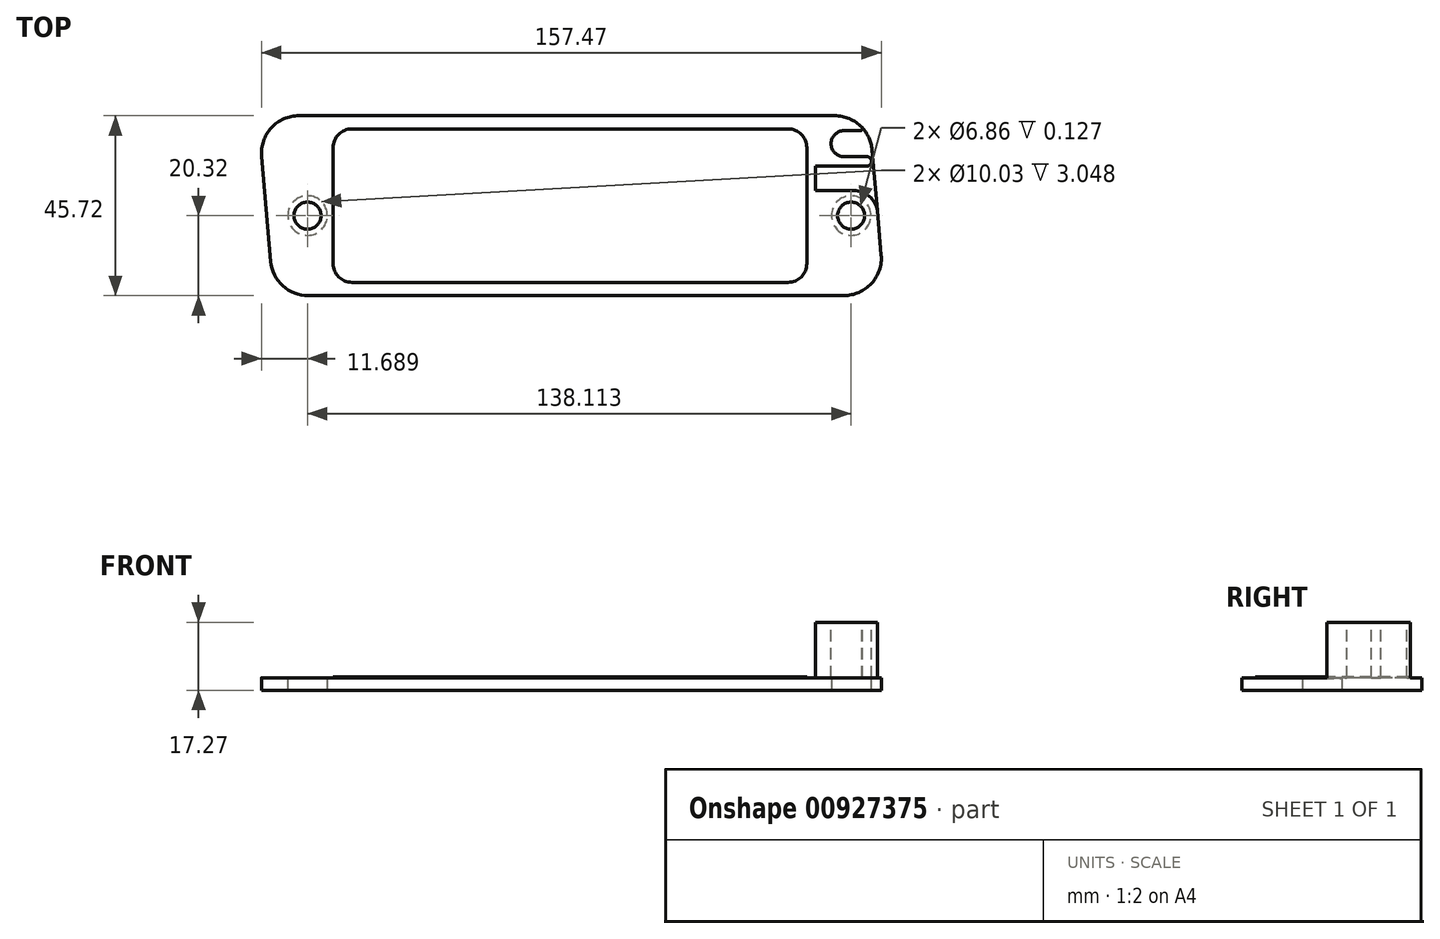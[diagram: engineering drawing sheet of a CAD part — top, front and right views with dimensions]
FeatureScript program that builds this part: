
annotation { "Feature Type Name" : "Feature", "Feature Type Description" : "" }
export const myFeature = defineFeature(function(context is Context, id is Id, definition is map)
    precondition{}
    {
        {
            var Q0;
            Q0=qCreatedBy(makeId("Top.planeOp"),FACE);
            var sketch = newSketch(context, id + "F0", { "sketchPlane" : qUnion([Q0])});
            skLineSegment(sketch, "E0.bottom", {"start": v(-68.04, 22.86) * mm, "end": v(68.04, 22.86) * mm});
            skLineSegment(sketch, "E0.top", {"start": v(-65.71, -22.86) * mm, "end": v(70.38, -22.86) * mm});
            skPoint(sketch, "E1", {"position": v(0, 22.86) * mm});
            skArc(sketch, "E2", {"start": v(77.53, 14.17) * mm, "mid": v(74.48, 20.36) * mm, "end": v(68.04, 22.86) * mm});
            skLineSegment(sketch, "E3", {"start": v(77.53, 14.17) * mm, "end": v(79.87, -12.5) * mm});
            skLineSegment(sketch, "E4", {"start": v(77.53, 14.17) * mm, "end": v(77.53, -3.79) * mm, "construction": true});
            skArc(sketch, "E5", {"start": v(70.38, -22.86) * mm, "mid": v(77.4, -19.77) * mm, "end": v(79.87, -12.5) * mm});
            skArc(sketch, "E6", {"start": v(-68.04, 22.86) * mm, "mid": v(-75.07, 19.77) * mm, "end": v(-77.53, 12.5) * mm});
            skLineSegment(sketch, "E7", {"start": v(-77.53, 12.5) * mm, "end": v(-75.2, -14.17) * mm});
            skLineSegment(sketch, "E8", {"start": v(-77.53, 12.5) * mm, "end": v(-77.53, -10.9) * mm, "construction": true});
            skArc(sketch, "E9", {"start": v(-75.2, -14.17) * mm, "mid": v(-72.15, -20.36) * mm, "end": v(-65.71, -22.86) * mm});
            skSolve(sketch);
        }
        {
            var Q0;
            Q0=makeQuery(id+"F0.imprint","IMPRINT",FACE,{"disambiguationData":[TD([[makeQuery(id+"F0.imprint","IMPRINT",EDGE,{"derivedFrom":sQuery(id+"F0.wireOp",EDGE,"E0.bottom")}),-1.0]])]});
            extrude(context, id + "F1", {"entities" : qUnion([Q0]), "depth" : 17.27 * mm, "offsetDistance" : 25.4 * mm});
        }
        {
            var Q0;
            Q0=makeQuery(id+"F1.opExtrude","CAP_FACE",FACE,{"disambiguationData":[OSD([sQuery(id+"F0.wireOp",EDGE,"E0.bottom"),sQuery(id+"F0.wireOp",EDGE,"E0.top"),sQuery(id+"F0.wireOp",EDGE,"E2"),sQuery(id+"F0.wireOp",EDGE,"E3"),sQuery(id+"F0.wireOp",EDGE,"E5"),sQuery(id+"F0.wireOp",EDGE,"E6"),sQuery(id+"F0.wireOp",EDGE,"E7"),sQuery(id+"F0.wireOp",EDGE,"E9")])],"isStart":false});
            var sketch = newSketch(context, id + "F2", { "sketchPlane" : qUnion([Q0])});
            skLineSegment(sketch, "E10.bottom", {"start": v(-54.61, 19.5) * mm, "end": v(56.2, 19.5) * mm});
            skLineSegment(sketch, "E10.top", {"start": v(-54.61, -19.5) * mm, "end": v(56.2, -19.5) * mm});
            skLineSegment(sketch, "E10.left", {"start": v(-59.37, 14.73) * mm, "end": v(-59.37, -14.73) * mm});
            skLineSegment(sketch, "E10.right", {"start": v(60.96, 14.73) * mm, "end": v(60.96, -14.73) * mm});
            skPoint(sketch, "E11", {"position": v(-59.37, 0) * mm});
            skPoint(sketch, "E12.visualSharp", {"position": v(-59.37, 19.5) * mm});
            skArc(sketch, "E12.filletArc", {"start": v(-54.61, 19.5) * mm, "mid": v(-57.98, 18.1) * mm, "end": v(-59.37, 14.73) * mm});
            skPoint(sketch, "E13.visualSharp", {"position": v(-59.37, -19.5) * mm});
            skArc(sketch, "E13.filletArc", {"start": v(-59.37, -14.73) * mm, "mid": v(-57.98, -18.1) * mm, "end": v(-54.61, -19.5) * mm});
            skPoint(sketch, "E14.visualSharp", {"position": v(60.96, -19.5) * mm});
            skArc(sketch, "E14.filletArc", {"start": v(56.2, -19.5) * mm, "mid": v(59.57, -18.1) * mm, "end": v(60.96, -14.73) * mm});
            skPoint(sketch, "E15.visualSharp", {"position": v(60.96, 19.5) * mm});
            skArc(sketch, "E15.filletArc", {"start": v(60.96, 14.73) * mm, "mid": v(59.57, 18.1) * mm, "end": v(56.2, 19.5) * mm});
            skPoint(sketch, "E16", {"position": v(0, -2.54) * mm});
            skSolve(sketch);
        }
        {
            var Q0;
            Q0=makeQuery(id+"F2.imprint","IMPRINT",FACE,{"disambiguationData":[TD([[makeQuery(id+"F2.imprint","IMPRINT",EDGE,{"derivedFrom":sQuery(id+"F2.wireOp",EDGE,"E10.bottom")}),-1.0]])]});
            extrude(context, id + "F3", {"entities" : qUnion([Q0]), "operationType" : NewBodyOperationType.REMOVE, "oppositeDirection" : true, "depth" : 13.84 * mm, "offsetDistance" : 25.4 * mm});
        }
        {
            var Q0;
            Q0=makeQuery(id+"F1.opExtrude","CAP_FACE",FACE,{"disambiguationData":[OSD([sQuery(id+"F0.wireOp",EDGE,"E0.bottom"),sQuery(id+"F0.wireOp",EDGE,"E0.top"),sQuery(id+"F0.wireOp",EDGE,"E2"),sQuery(id+"F0.wireOp",EDGE,"E3"),sQuery(id+"F0.wireOp",EDGE,"E5"),sQuery(id+"F0.wireOp",EDGE,"E6"),sQuery(id+"F0.wireOp",EDGE,"E7"),sQuery(id+"F0.wireOp",EDGE,"E9")])],"isStart":false});
            var sketch = newSketch(context, id + "F4", { "sketchPlane" : qUnion([Q0])});
            skLineSegment(sketch, "E17", {"start": v(-63.18, 10.03) * mm, "end": v(-76.22, 10.03) * mm});
            skLineSegment(sketch, "E18", {"start": v(-63.18, 10.03) * mm, "end": v(-63.18, 3.8) * mm});
            skLineSegment(sketch, "E19", {"start": v(-63.18, 3.81) * mm, "end": v(-72.92, 3.81) * mm});
            skLineSegment(sketch, "E20", {"start": v(-63.18, -8.25) * mm, "end": v(-72.7, -8.26) * mm});
            skPoint(sketch, "E21", {"position": v(0, -2.54) * mm});
            skArc(sketch, "E22", {"start": v(-72.92, 3.81) * mm, "mid": v(-76.24, -2.28) * mm, "end": v(-72.7, -8.25) * mm});
            skPoint(sketch, "E23", {"position": v(-76.24, -2.28) * mm});
            skLineSegment(sketch, "E24", {"start": v(-63.18, -8.26) * mm, "end": v(-63.18, -14.73) * mm});
            skArc(sketch, "E25", {"start": v(-63.18, -14.73) * mm, "mid": v(-60.8, -20.48) * mm, "end": v(-55.05, -22.86) * mm});
            skLineSegment(sketch, "E26", {"start": v(-76.22, 12.45) * mm, "end": v(-70.42, 12.45) * mm});
            skArc(sketch, "E27", {"start": v(-76.22, 12.45) * mm, "mid": v(-77.42, 11.24) * mm, "end": v(-76.22, 10.03) * mm});
            skPoint(sketch, "E28", {"position": v(-77.42, 11.24) * mm});
            skArc(sketch, "E29", {"start": v(-70.42, 12.45) * mm, "mid": v(-67.12, 15.75) * mm, "end": v(-70.42, 19.05) * mm});
            skLineSegment(sketch, "E30", {"start": v(-70.42, 19.05) * mm, "end": v(-74.57, 19.05) * mm});
            skArc(sketch, "E31", {"start": v(-68.04, 22.86) * mm, "mid": v(-71.8, 22.1) * mm, "end": v(-74.94, 19.9) * mm});
            skLineSegment(sketch, "E32", {"start": v(-68.04, 22.86) * mm, "end": v(-80.53, 22.86) * mm});
            skLineSegment(sketch, "E33", {"start": v(-80.53, 22.86) * mm, "end": v(-80.53, -22.86) * mm});
            skLineSegment(sketch, "E34", {"start": v(-80.53, -22.86) * mm, "end": v(-55.05, -22.86) * mm});
            skPoint(sketch, "E35.visualSharp", {"position": v(-75.66, 19.05) * mm});
            skArc(sketch, "E35.filletArc", {"start": v(-74.94, 19.9) * mm, "mid": v(-75.04, 19.36) * mm, "end": v(-74.57, 19.05) * mm});
            skPoint(sketch, "E36", {"position": v(-67.12, 15.75) * mm});
            skLineSegment(sketch, "E37", {"start": v(0, 45.68) * mm, "end": v(0, -48.97) * mm, "construction": true});
            skArc(sketch, "E38.MirrorCS", {"start": v(74.94, 19.9) * mm, "mid": v(75.04, 19.36) * mm, "end": v(74.57, 19.05) * mm});
            skLineSegment(sketch, "E39.MirrorCS", {"start": v(70.42, 19.05) * mm, "end": v(74.57, 19.05) * mm});
            skArc(sketch, "E40.MirrorCS", {"start": v(76.22, 12.45) * mm, "mid": v(77.42, 11.24) * mm, "end": v(76.22, 10.03) * mm});
            skLineSegment(sketch, "E41.MirrorCS", {"start": v(63.18, -8.25) * mm, "end": v(72.7, -8.25) * mm});
            skLineSegment(sketch, "E42.MirrorCS", {"start": v(63.18, 3.81) * mm, "end": v(72.92, 3.81) * mm});
            skLineSegment(sketch, "E43.MirrorCS", {"start": v(76.22, 12.45) * mm, "end": v(70.42, 12.45) * mm});
            skArc(sketch, "E44.MirrorCS", {"start": v(70.42, 12.45) * mm, "mid": v(67.12, 15.75) * mm, "end": v(70.42, 19.05) * mm});
            skLineSegment(sketch, "E45.MirrorCS", {"start": v(80.53, 22.86) * mm, "end": v(80.53, -22.86) * mm});
            skPoint(sketch, "E46.MirrorP", {"position": v(67.12, 15.75) * mm});
            skPoint(sketch, "E47.MirrorP", {"position": v(75.66, 19.05) * mm});
            skArc(sketch, "E48.MirrorCS", {"start": v(63.18, -14.73) * mm, "mid": v(60.8, -20.48) * mm, "end": v(55.05, -22.86) * mm});
            skPoint(sketch, "E49.MirrorP", {"position": v(77.42, 11.24) * mm});
            skArc(sketch, "E50.MirrorCS", {"start": v(72.92, 3.81) * mm, "mid": v(78.96, -2.33) * mm, "end": v(72.7, -8.26) * mm});
            skLineSegment(sketch, "E51.MirrorCS", {"start": v(63.18, 10.03) * mm, "end": v(76.22, 10.03) * mm});
            skLineSegment(sketch, "E52.MirrorCS", {"start": v(63.18, 10.03) * mm, "end": v(63.18, 3.8) * mm});
            skLineSegment(sketch, "E53.MirrorCS", {"start": v(80.53, -22.86) * mm, "end": v(55.05, -22.86) * mm});
            skLineSegment(sketch, "E54.MirrorCS", {"start": v(63.18, -8.26) * mm, "end": v(63.18, -14.73) * mm});
            skLineSegment(sketch, "E55.MirrorCS", {"start": v(68.04, 22.86) * mm, "end": v(80.53, 22.86) * mm});
            skArc(sketch, "E56.MirrorCS", {"start": v(68.04, 22.86) * mm, "mid": v(71.8, 22.1) * mm, "end": v(74.94, 19.9) * mm});
            skPoint(sketch, "E57", {"position": v(78.96, -2.11) * mm});
            skPoint(sketch, "E57.positionSnap0", {"position": v(78.96, -2.33) * mm});
            skSolve(sketch);
        }
        {
            var Q0;
            {var subQ8=sQuery(id+"F4.wireOp",EDGE,"E31");Q0=makeQuery(id+"F4.imprint","IMPRINT",FACE,{"disambiguationData":[TD([[makeQuery(id+"F4.imprint","IMPRINT",EDGE,{"derivedFrom":subQ8}),-1.0]])]});}
            var Q1;
            {var subQ1=sQuery(id+"F4.wireOp",EDGE,"E26");Q1=makeQuery(id+"F4.imprint","IMPRINT",FACE,{"disambiguationData":[TD([[makeQuery(id+"F4.imprint","IMPRINT",EDGE,{"derivedFrom":subQ1}),1.0]])]});}
            var Q2;
            {var subQ5=sQuery(id+"F4.wireOp",EDGE,"E17");Q2=makeQuery(id+"F4.imprint","IMPRINT",FACE,{"disambiguationData":[TD([[makeQuery(id+"F4.imprint","IMPRINT",EDGE,{"derivedFrom":subQ5}),1.0]])]});}
            var Q3;
            {var subQ4=sQuery(id+"F4.wireOp",EDGE,"E20");Q3=makeQuery(id+"F4.imprint","IMPRINT",FACE,{"disambiguationData":[TD([[makeQuery(id+"F4.imprint","IMPRINT",EDGE,{"derivedFrom":subQ4}),1.0]])]});}
            var Q4;
            {var subQ0=sQuery(id+"F4.wireOp",EDGE,"85b55b84-e163-4874-8427-2380d430c36f0.MirrorCS");Q4=makeQuery(id+"F4.imprint","IMPRINT",FACE,{"disambiguationData":[TD([[makeQuery(id+"F4.imprint","IMPRINT",EDGE,{"derivedFrom":subQ0}),1.0]])]});}
            var Q5;
            {var subQ3=sQuery(id+"F4.wireOp",EDGE,"af567ee6-1c98-437c-b070-15830dda8ad00.MirrorCS");Q5=makeQuery(id+"F4.imprint","IMPRINT",FACE,{"disambiguationData":[TD([[makeQuery(id+"F4.imprint","IMPRINT",EDGE,{"derivedFrom":subQ3}),-1.0]])]});}
            var Q6;
            {var subQ4=sQuery(id+"F4.wireOp",EDGE,"E41.MirrorCS");Q6=makeQuery(id+"F4.imprint","IMPRINT",FACE,{"disambiguationData":[TD([[makeQuery(id+"F4.imprint","IMPRINT",EDGE,{"derivedFrom":subQ4}),-1.0]])]});}
            var Q7;
            {var subQ3=sQuery(id+"F4.wireOp",EDGE,"E38.MirrorCS");Q7=makeQuery(id+"F4.imprint","IMPRINT",FACE,{"disambiguationData":[TD([[makeQuery(id+"F4.imprint","IMPRINT",EDGE,{"derivedFrom":subQ3}),1.0]])]});}
            extrude(context, id + "F5", {"entities" : qUnion([Q0, Q1, Q2, Q3, Q4, Q5, Q6, Q7]), "operationType" : NewBodyOperationType.REMOVE, "oppositeDirection" : true, "depth" : 14.1 * mm, "offsetDistance" : 25.4 * mm});
        }
        {
            var Q0;
            Q0=makeQuery(id+"F1.opExtrude","CAP_FACE",FACE,{"disambiguationData":[OSD([sQuery(id+"F0.wireOp",EDGE,"E0.bottom"),sQuery(id+"F0.wireOp",EDGE,"E0.top"),sQuery(id+"F0.wireOp",EDGE,"E2"),sQuery(id+"F0.wireOp",EDGE,"E3"),sQuery(id+"F0.wireOp",EDGE,"E5"),sQuery(id+"F0.wireOp",EDGE,"E6"),sQuery(id+"F0.wireOp",EDGE,"E7"),sQuery(id+"F0.wireOp",EDGE,"E9")])],"isStart":true});
            var sketch = newSketch(context, id + "F6", { "sketchPlane" : qUnion([Q0])});
            skLineSegment(sketch, "E58", {"start": v(72.23, 2.54) * mm, "end": v(-65.88, 2.54) * mm, "construction": true});
            skPoint(sketch, "E59", {"position": v(0, 2.54) * mm});
            skSolve(sketch);
        }
        {
            var Q0;
            Q0=sQuery(id+"F6.wireOp",VERTEX,"E58.start");
            var Q1;
            Q1=sQuery(id+"F6.wireOp",VERTEX,"E58.end");
            var Q2;
            Q2=makeQuery(id+"F1.opExtrude","SWEPT_BODY",BODY,{"disambiguationData":[OSD([sQuery(id+"F0.wireOp",EDGE,"E0.bottom"),sQuery(id+"F0.wireOp",EDGE,"E0.top"),sQuery(id+"F0.wireOp",EDGE,"E2"),sQuery(id+"F0.wireOp",EDGE,"E3"),sQuery(id+"F0.wireOp",EDGE,"E5"),sQuery(id+"F0.wireOp",EDGE,"E6"),sQuery(id+"F0.wireOp",EDGE,"E7"),sQuery(id+"F0.wireOp",EDGE,"E9")])]});
            hole(context, id + "F7", {"style" : HoleStyle.C_BORE, "endStyle" : HoleEndStyle.THROUGH, "holeDiameter" : 6.86 * mm, "cBoreDiameter" : 10.03 * mm, "cBoreDepth" : 3.05 * mm, "majorDiameter" : 6.35 * mm, "isTappedThrough" : true, "tappedDepth" : 12.7 * mm, "tapClearance" : 3, "startFromSketch" : true, "locations" : qUnion([Q0, Q1]), "scope" : qUnion([Q2])});
        }
    });
